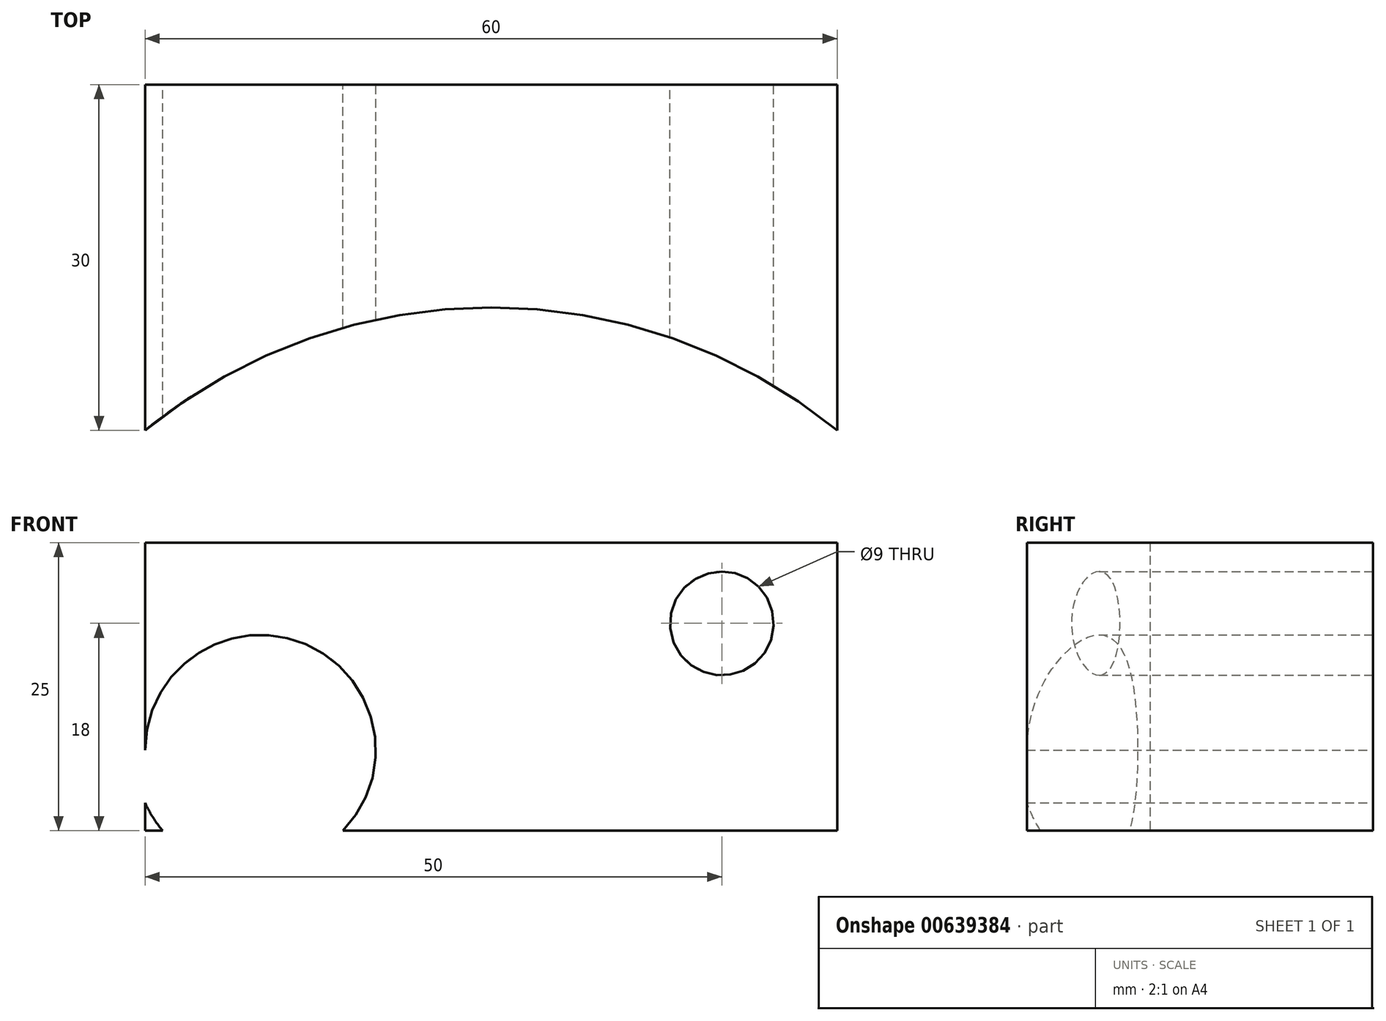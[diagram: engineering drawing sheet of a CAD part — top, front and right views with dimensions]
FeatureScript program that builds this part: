
annotation { "Feature Type Name" : "Feature", "Feature Type Description" : "" }
export const myFeature = defineFeature(function(context is Context, id is Id, definition is map)
    precondition{}
    {
        {
            var Q0;
            Q0=qCreatedBy(makeId("Top.planeOp"),FACE);
            var sketch = newSketch(context, id + "F0", { "sketchPlane" : qUnion([Q0])});
            skLineSegment(sketch, "E0.bottom", {"start": v(-30, 15) * mm, "end": v(30, 15) * mm});
            skLineSegment(sketch, "E0.top", {"start": v(-30, -15) * mm, "end": v(30, -15) * mm});
            skLineSegment(sketch, "E0.left", {"start": v(-30, 15) * mm, "end": v(-30, -15) * mm});
            skLineSegment(sketch, "E0.right", {"start": v(30, 15) * mm, "end": v(30, -15) * mm});
            skPoint(sketch, "E0.middle", {"position": v(0, 0) * mm});
            skArc(sketch, "E1", {"start": v(-30, -15) * mm, "mid": v(0, -4.32) * mm, "end": v(30, -15) * mm});
            skSolve(sketch);
        }
        {
            var Q0;
            Q0=makeQuery(id+"F0.imprint","IMPRINT",FACE,{"disambiguationData":[TD([[makeQuery(id+"F0.imprint","IMPRINT",EDGE,{"derivedFrom":sQuery(id+"F0.wireOp",EDGE,"E0.bottom")}),-1.0]])]});
            extrude(context, id + "F1", {"entities" : qUnion([Q0]), "depth" : 25 * mm, "offsetDistance" : 25 * mm});
        }
        {
            var Q0;
            Q0=makeQuery(id+"F1.opExtrude","SWEPT_FACE",FACE,{"disambiguationData":[OSD([sQuery(id+"F0.wireOp",EDGE,"E0.bottom")])]});
            var sketch = newSketch(context, id + "F2", { "sketchPlane" : qUnion([Q0])});
            skLineSegment(sketch, "E2", {"start": v(-30, 7) * mm, "end": v(30, 7) * mm, "construction": true});
            skLineSegment(sketch, "E3", {"start": v(-30, 18) * mm, "end": v(30, 18) * mm, "construction": true});
            skLineSegment(sketch, "E4", {"start": v(-20, 25) * mm, "end": v(-20, 0) * mm, "construction": true});
            skLineSegment(sketch, "E5", {"start": v(20, 25) * mm, "end": v(20, 0) * mm, "construction": true});
            skCircle(sketch, "E6", {"center": v(20, 7) * mm, "radius": 10 * mm});
            skCircle(sketch, "E7", {"center": v(-20, 18) * mm, "radius": 4.5 * mm});
            skCircle(sketch, "E8.0", {"center": v(20, 7) * mm, "radius": 11 * mm});
            skCircle(sketch, "E9.0", {"center": v(-20, 18) * mm, "radius": 14.5 * mm});
            skSolve(sketch);
        }
        {
            var Q0;
            {var subQ0=sQuery(id+"F2.wireOp",EDGE,"E6");var subQ1=sQuery(id+"F0.wireOp",EDGE,"E0.bottom");var subQ2=makeQuery(id+"F1.opExtrude","CAP_EDGE",EDGE,{"disambiguationData":[OSD([subQ1])],"isStart":true});var subQ3=makeQuery(id+"F2.imprint","INTERSECT",VERTEX,{"disambiguationData":[OD(0.0)],"derivedFrom":[subQ2,subQ0]});Q0=makeQuery(id+"F2.imprint","IMPRINT",FACE,{"disambiguationData":[TD([[makeQuery(id+"F2.imprint","IMPRINT",EDGE,{"disambiguationData":[TD([[subQ3,1.0]])],"derivedFrom":subQ2}),-1.0]])]});}
            var Q1;
            {var subQ0=sQuery(id+"F2.wireOp",EDGE,"E6");var subQ1=makeQuery(id+"F1.opExtrude","CAP_EDGE",EDGE,{"disambiguationData":[OSD([sQuery(id+"F0.wireOp",EDGE,"E0.bottom")])],"isStart":true});var subQ2=makeQuery(id+"F2.imprint","INTERSECT",VERTEX,{"disambiguationData":[OD(0.0)],"derivedFrom":[subQ1,subQ0]});Q1=makeQuery(id+"F2.imprint","IMPRINT",FACE,{"disambiguationData":[TD([[makeQuery(id+"F2.imprint","IMPRINT",EDGE,{"disambiguationData":[TD([[subQ2,-1.0]])],"derivedFrom":subQ0}),1.0]])]});}
            var Q2;
            Q2=makeQuery(id+"F2.imprint","IMPRINT",FACE,{"disambiguationData":[TD([[makeQuery(id+"F2.imprint","IMPRINT",EDGE,{"derivedFrom":sQuery(id+"F2.wireOp",EDGE,"E7")}),1.0]])]});
            var Q3;
            Q3=makeQuery(id+"F1.opExtrude","SWEPT_FACE",FACE,{"disambiguationData":[OSD([sQuery(id+"F0.wireOp",EDGE,"E1")])]});
            extrude(context, id + "F3", {"entities" : qUnion([Q0, Q1, Q2]), "operationType" : NewBodyOperationType.REMOVE, "endBound" : BoundingType.UP_TO_SURFACE, "oppositeDirection" : true, "depth" : 25 * mm, "endBoundEntityFace" : qUnion([Q3]), "offsetDistance" : 25 * mm});
        }
        {
            var Q0;
            Q0=makeQuery(id+"F1.opExtrude","SWEPT_FACE",FACE,{"disambiguationData":[OSD([sQuery(id+"F0.wireOp",EDGE,"E0.right")])]});
            var sketch = newSketch(context, id + "F4", { "sketchPlane" : qUnion([Q0])});
            skCircle(sketch, "E10", {"center": v(-15, 25) * mm, "radius": 5 * mm});
            skSolve(sketch);
        }
        {
            var Q0;
            {var subQ0=sQuery(id+"F0.wireOp",EDGE,"E0.right");var subQ1=makeQuery(id+"F1.opExtrude","CAP_EDGE",EDGE,{"disambiguationData":[OSD([subQ0])],"isStart":true});Q0=makeQuery(id+"F4.imprint","IMPRINT",FACE,{"disambiguationData":[TD([[makeQuery(id+"F4.imprint","IMPRINT",EDGE,{"derivedFrom":subQ1}),-1.0]])]});}
            var Q1;
            {var subQ0=sQuery(id+"F4.wireOp",EDGE,"E10");var subQ1=sQuery(id+"F0.wireOp",EDGE,"E0.right");var subQ4=makeQuery(id+"F1.opExtrude","CAP_EDGE",EDGE,{"disambiguationData":[OSD([subQ1])],"isStart":false});var subQ5=makeQuery(id+"F4.imprint","INTERSECT",VERTEX,{"derivedFrom":[subQ4,subQ0]});Q1=makeQuery(id+"F4.imprint","IMPRINT",FACE,{"disambiguationData":[TD([[makeQuery(id+"F4.imprint","IMPRINT",EDGE,{"disambiguationData":[TD([[subQ5,1.0]])],"derivedFrom":subQ0}),1.0]])]});}
            cPlane(context, id + "F5", {"entities" : qUnion([Q0, Q1]), "cplaneType" : CPlaneType.MID_PLANE, "offset" : 25 * mm, "width" : 150 * mm, "height" : 150 * mm});
        }
    });
